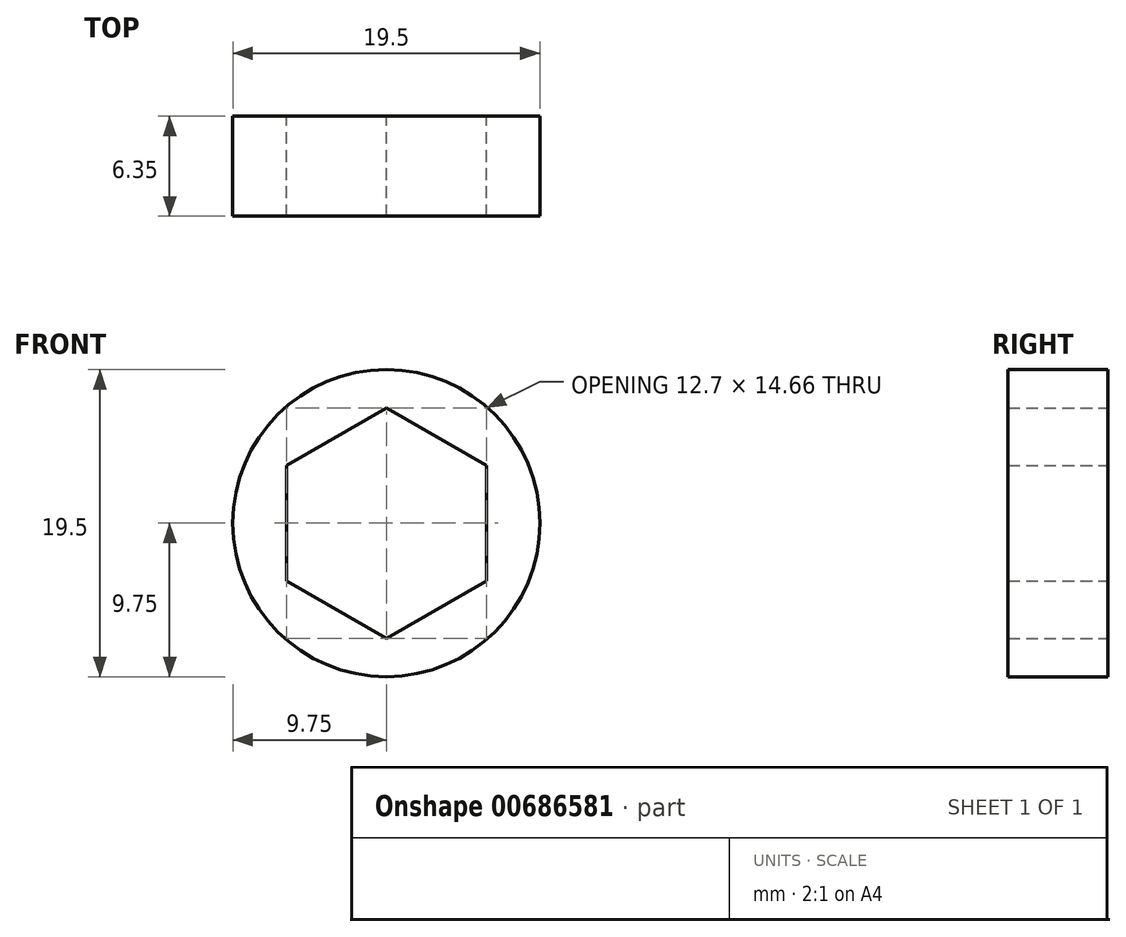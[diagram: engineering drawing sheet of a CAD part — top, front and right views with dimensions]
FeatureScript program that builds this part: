
annotation { "Feature Type Name" : "Feature", "Feature Type Description" : "" }
export const myFeature = defineFeature(function(context is Context, id is Id, definition is map)
    precondition{}
    {
        {
            var Q0;
            Q0=qCreatedBy(makeId("Front.planeOp"),FACE);
            var sketch = newSketch(context, id + "F0", { "sketchPlane" : qUnion([Q0])});
            skCircle(sketch, "E0", {"center": v(0, 0) * mm, "radius": 9.75 * mm});
            skCircle(sketch, "E1.cCircle", {"center": v(0, 0) * mm, "radius": 6.35 * mm, "construction": true});
            skLineSegment(sketch, "E1.0", {"start": v(6.35, 3.67) * mm, "end": v(6.35, -3.67) * mm});
            skLineSegment(sketch, "E1.1", {"start": v(6.35, -3.67) * mm, "end": v(0, -7.33) * mm});
            skLineSegment(sketch, "E1.2", {"start": v(0, -7.33) * mm, "end": v(-6.35, -3.67) * mm});
            skLineSegment(sketch, "E1.3", {"start": v(-6.35, -3.67) * mm, "end": v(-6.35, 3.67) * mm});
            skLineSegment(sketch, "E1.4", {"start": v(-6.35, 3.67) * mm, "end": v(0, 7.33) * mm});
            skLineSegment(sketch, "E1.5", {"start": v(0, 7.33) * mm, "end": v(6.35, 3.67) * mm});
            skPoint(sketch, "E1.0.midPoint", {"position": v(6.35, 0) * mm});
            skSolve(sketch);
        }
        {
            var Q0;
            Q0=makeQuery(id+"F0.imprint","IMPRINT",FACE,{"disambiguationData":[TD([[makeQuery(id+"F0.imprint","IMPRINT",EDGE,{"derivedFrom":sQuery(id+"F0.wireOp",EDGE,"E0")}),1.0]])]});
            extrude(context, id + "F1", {"entities" : qUnion([Q0]), "depth" : 6.35 * mm, "offsetDistance" : 25.4 * mm});
        }
    });
